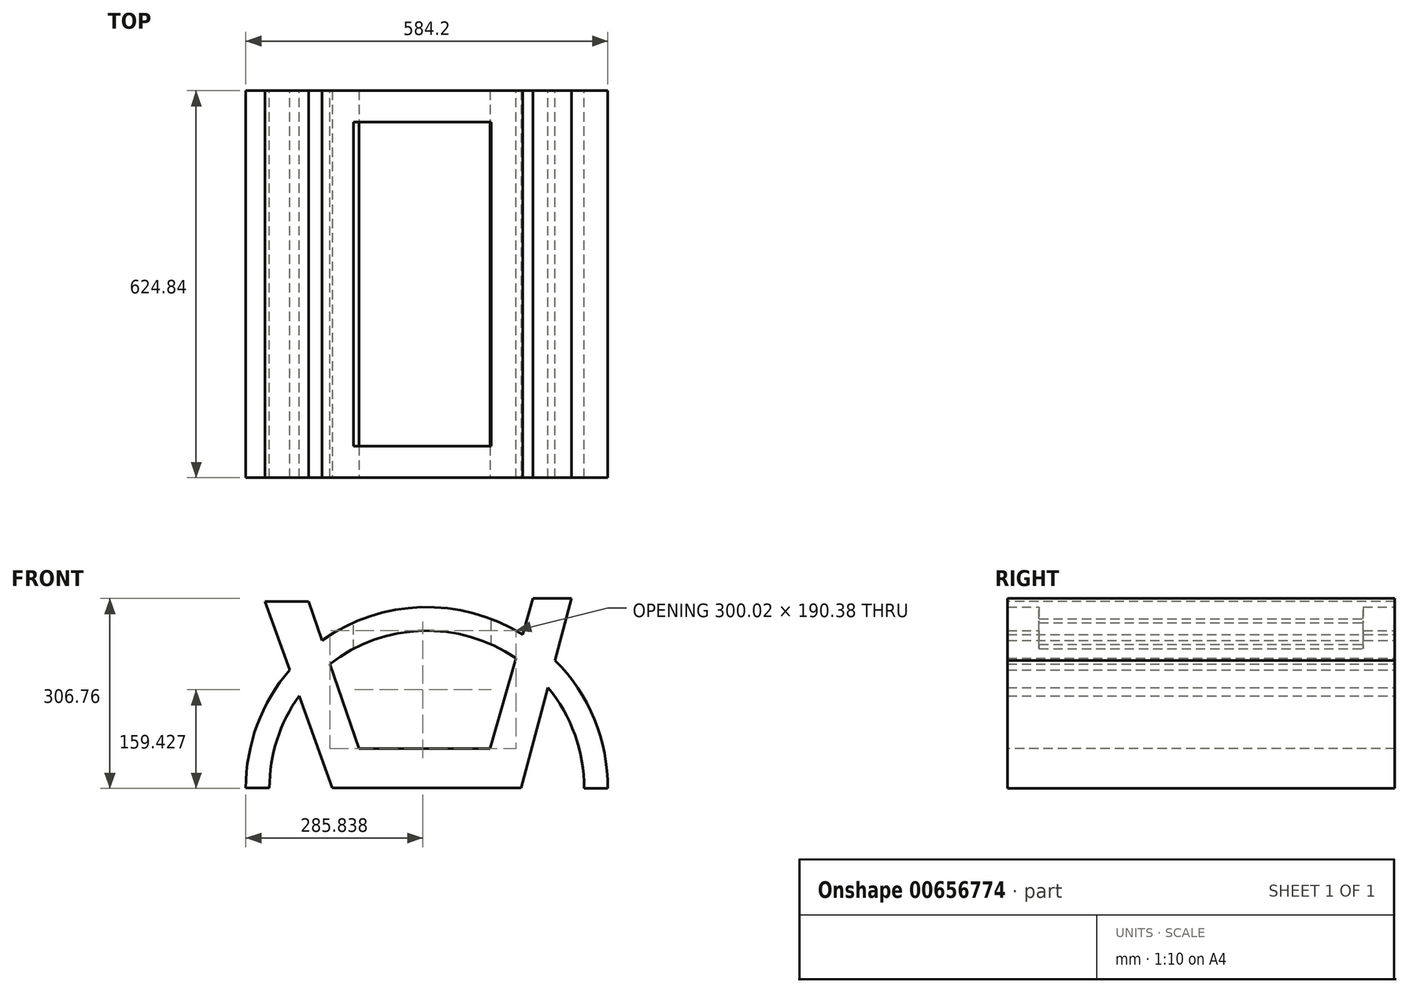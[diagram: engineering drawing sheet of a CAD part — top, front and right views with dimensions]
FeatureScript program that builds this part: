
annotation { "Feature Type Name" : "Feature", "Feature Type Description" : "" }
export const myFeature = defineFeature(function(context is Context, id is Id, definition is map)
    precondition{}
    {
        {
            var Q0;
            Q0=qCreatedBy(makeId("Front.planeOp"),FACE);
            var sketch = newSketch(context, id + "F0", { "sketchPlane" : qUnion([Q0])});
            skArc(sketch, "E0", {"start": v(401.64, -301.65) * mm, "mid": v(109.9, -8.81) * mm, "end": v(-182.56, -300.91) * mm});
            skArc(sketch, "E1", {"start": v(363.54, -301.65) * mm, "mid": v(109.9, -46.91) * mm, "end": v(-144.46, -300.91) * mm});
            skLineSegment(sketch, "E2", {"start": v(401.64, -301.65) * mm, "end": v(363.54, -301.65) * mm});
            skLineSegment(sketch, "E3", {"start": v(-182.56, -300.91) * mm, "end": v(-144.46, -300.91) * mm});
            skPoint(sketch, "E4.startSnap0", {"position": v(109.9, -8.81) * mm});
            skSolve(sketch);
        }
        {
            var Q0;
            Q0 = qSketchRegion(id + "F0", true);
            extrude(context, id + "F1", {"entities" : qUnion([Q0]), "depth" : 624.84 * mm, "offsetDistance" : 25.4 * mm});
        }
        {
            var Q0;
            Q0=makeQuery(id+"F1.opExtrude","CAP_FACE",FACE,{"disambiguationData":[OSD([sQuery(id+"F0.wireOp",EDGE,"E0"),sQuery(id+"F0.wireOp",EDGE,"E1"),sQuery(id+"F0.wireOp",EDGE,"E2"),sQuery(id+"F0.wireOp",EDGE,"E3")])],"isStart":false});
            var sketch = newSketch(context, id + "F2", { "sketchPlane" : qUnion([Q0])});
            skLineSegment(sketch, "E5", {"start": v(261.94, -300.91) * mm, "end": v(342.9, 5.1) * mm});
            skLineSegment(sketch, "E6", {"start": v(342.9, 5.1) * mm, "end": v(280.66, 5.1) * mm});
            skLineSegment(sketch, "E7", {"start": v(280.66, 5.1) * mm, "end": v(211.94, -237.41) * mm});
            skLineSegment(sketch, "E8", {"start": v(211.94, -237.41) * mm, "end": v(0, -237.41) * mm});
            skLineSegment(sketch, "E9", {"start": v(0, -237.41) * mm, "end": v(-81.14, 0) * mm});
            skLineSegment(sketch, "E10", {"start": v(261.94, -300.91) * mm, "end": v(-42.86, -300.91) * mm});
            skLineSegment(sketch, "E11", {"start": v(-42.86, -300.91) * mm, "end": v(-151.6, 0) * mm});
            skLineSegment(sketch, "E12", {"start": v(-151.6, 0) * mm, "end": v(-81.14, 0) * mm});
            skSolve(sketch);
        }
        {
            var Q0;
            Q0 = qSketchRegion(id + "F2", true);
            extrude(context, id + "F3", {"entities" : qUnion([Q0]), "operationType" : NewBodyOperationType.ADD, "oppositeDirection" : true, "depth" : 624.84 * mm, "offsetDistance" : 25.4 * mm});
        }
        {
            var Q0;
            Q0=makeQuery(id+"F3.opExtrude","SWEPT_FACE",FACE,{"disambiguationData":[OSD([sQuery(id+"F2.wireOp",EDGE,"E6")])]});
            var sketch = newSketch(context, id + "F4", { "sketchPlane" : qUnion([Q0])});
            skLineSegment(sketch, "E13.bottom", {"start": v(-8.87, -50.8) * mm, "end": v(213.37, -50.8) * mm});
            skLineSegment(sketch, "E13.top", {"start": v(-8.87, -574.04) * mm, "end": v(213.37, -574.04) * mm});
            skLineSegment(sketch, "E13.left", {"start": v(-8.87, -50.8) * mm, "end": v(-8.87, -574.04) * mm});
            skLineSegment(sketch, "E13.right", {"start": v(213.37, -50.8) * mm, "end": v(213.37, -574.04) * mm});
            skSolve(sketch);
        }
        {
            var Q0;
            Q0=makeQuery(id+"F4.imprint","IMPRINT",FACE,{"disambiguationData":[TD([[makeQuery(id+"F4.imprint","IMPRINT",EDGE,{"derivedFrom":sQuery(id+"F4.wireOp",EDGE,"E13.bottom")}),-1.0]])]});
            extrude(context, id + "F5", {"entities" : qUnion([Q0]), "operationType" : NewBodyOperationType.REMOVE, "oppositeDirection" : true, "depth" : 99.06 * mm, "offsetDistance" : 25.4 * mm});
        }
    });
